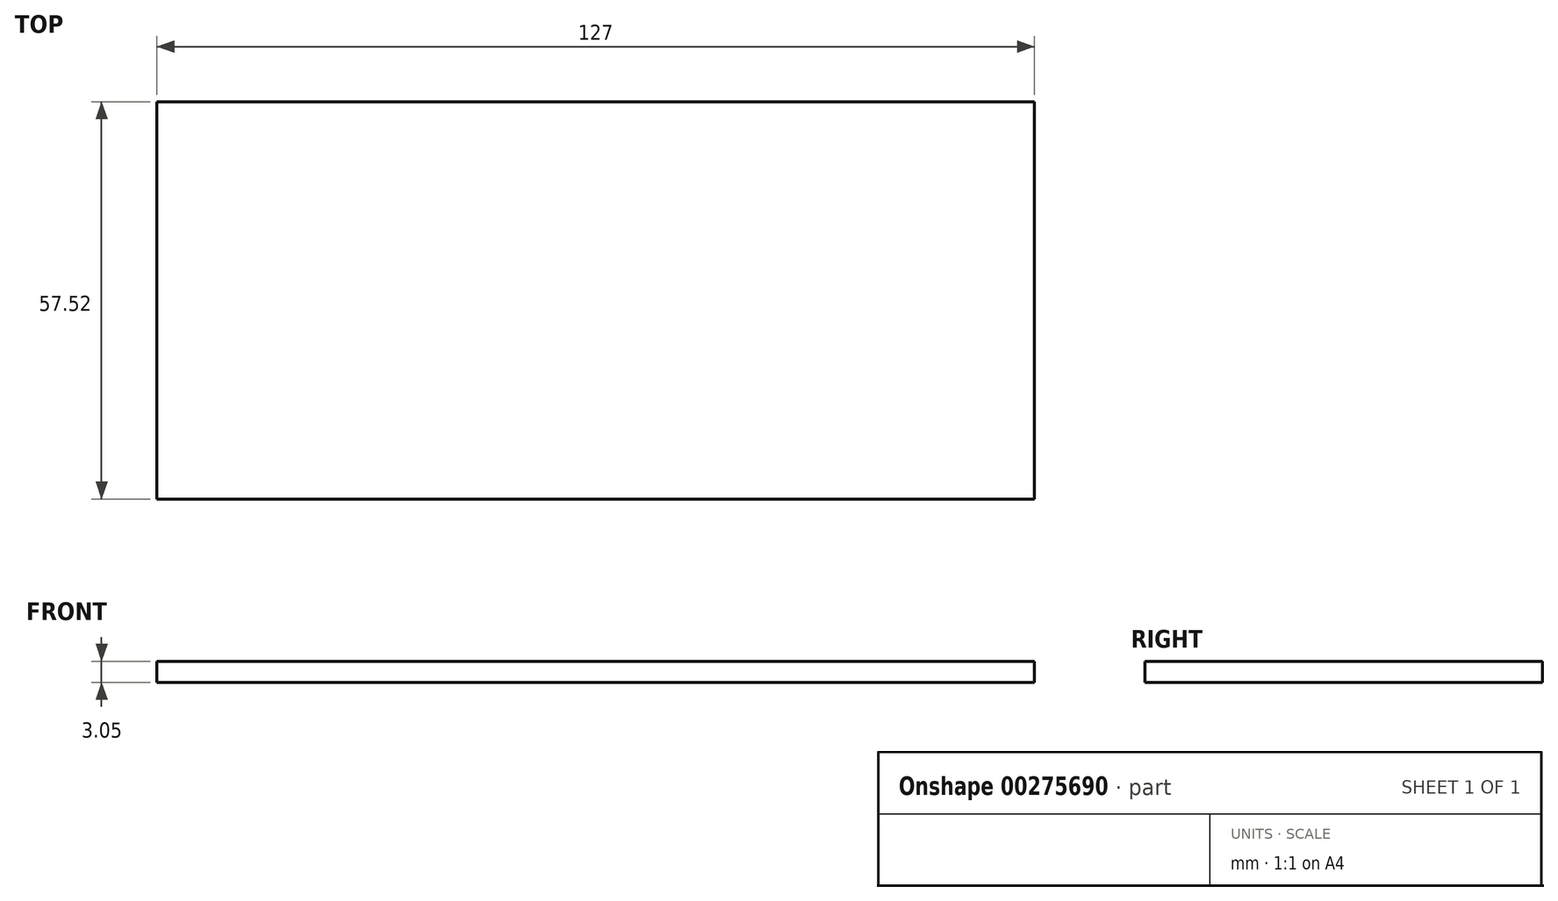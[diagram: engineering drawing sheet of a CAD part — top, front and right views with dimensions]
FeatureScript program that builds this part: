
annotation { "Feature Type Name" : "Feature", "Feature Type Description" : "" }
export const myFeature = defineFeature(function(context is Context, id is Id, definition is map)
    precondition{}
    {
        {
            var Q0;
            Q0=qCreatedBy(makeId("Top.planeOp"),FACE);
            var sketch = newSketch(context, id + "F0", { "sketchPlane" : qUnion([Q0])});
            skLineSegment(sketch, "E0.bottom", {"start": v(0, 74.97) * mm, "end": v(127, 74.97) * mm});
            skLineSegment(sketch, "E0.top", {"start": v(0, 17.45) * mm, "end": v(127, 17.45) * mm});
            skLineSegment(sketch, "E0.left", {"start": v(0, 74.97) * mm, "end": v(0, 17.45) * mm});
            skLineSegment(sketch, "E0.right", {"start": v(127, 74.97) * mm, "end": v(127, 17.45) * mm});
            skSolve(sketch);
        }
        {
            var Q0;
            Q0=makeQuery(id+"F0.imprint","IMPRINT",FACE,{"disambiguationData":[TD([[makeQuery(id+"F0.imprint","IMPRINT",EDGE,{"derivedFrom":sQuery(id+"F0.wireOp",EDGE,"E0.bottom")}),-1.0]])]});
            extrude(context, id + "F1", {"entities" : qUnion([Q0]), "depth" : 3.05 * mm});
        }
    });
